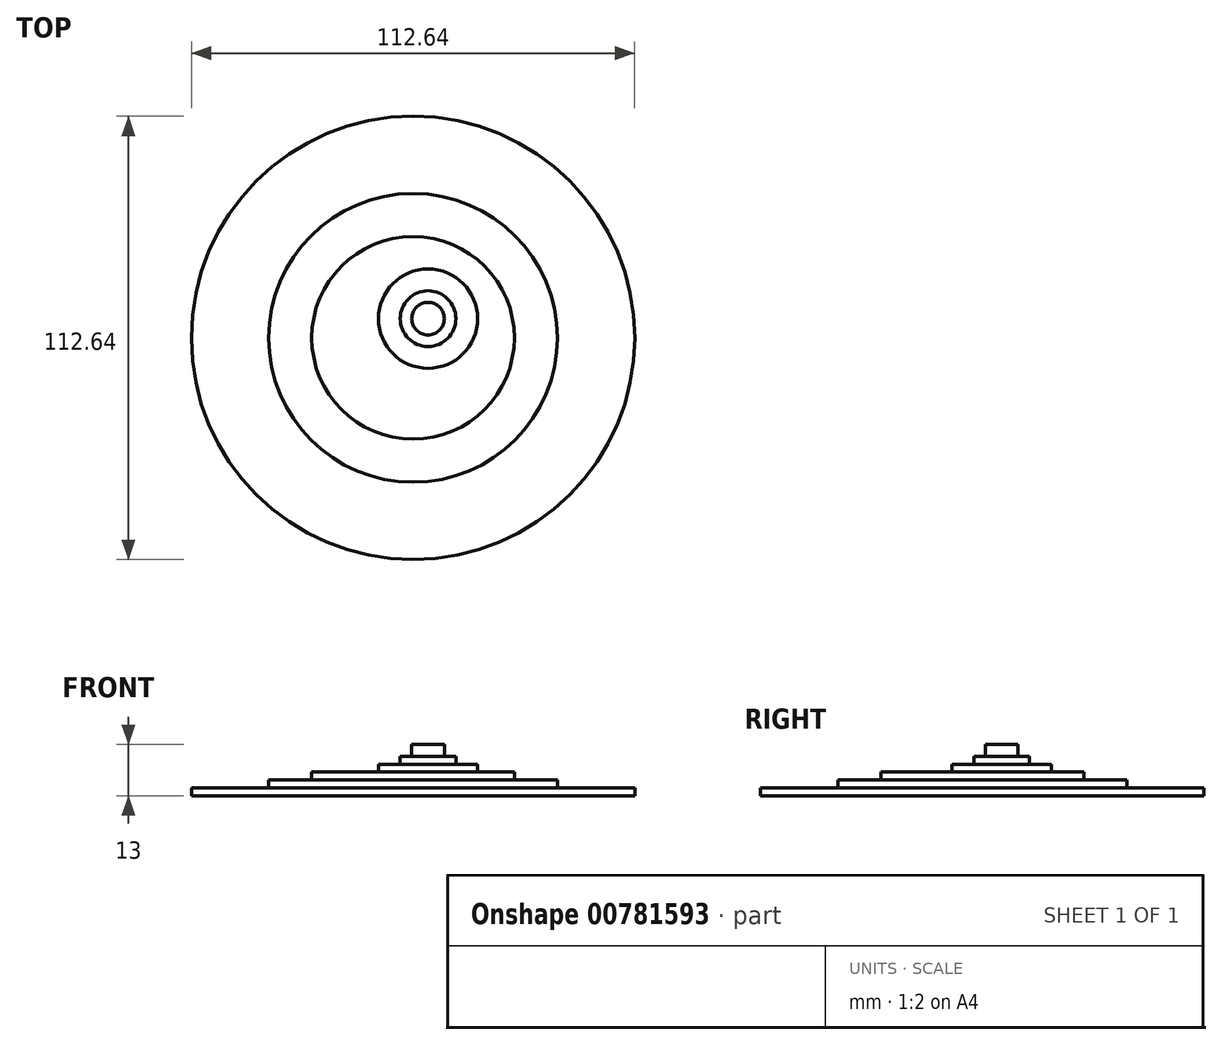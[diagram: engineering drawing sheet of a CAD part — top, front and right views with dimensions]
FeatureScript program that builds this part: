
annotation { "Feature Type Name" : "Feature", "Feature Type Description" : "" }
export const myFeature = defineFeature(function(context is Context, id is Id, definition is map)
    precondition{}
    {
        {
            var Q0;
            Q0=qCreatedBy(makeId("Top.planeOp"),FACE);
            var sketch = newSketch(context, id + "F0", { "sketchPlane" : qUnion([Q0])});
            skCircle(sketch, "E0", {"center": v(0, 0) * mm, "radius": 56.32 * mm});
            skSolve(sketch);
        }
        {
            var Q0;
            Q0=makeQuery(id+"F0.imprint","IMPRINT",FACE,{"disambiguationData":[TD([[makeQuery(id+"F0.imprint","IMPRINT",EDGE,{"derivedFrom":sQuery(id+"F0.wireOp",EDGE,"E0")}),1.0]])]});
            extrude(context, id + "F1", {"entities" : qUnion([Q0]), "depth" : 2 * mm, "offsetDistance" : 25.4 * mm});
        }
        {
            var Q0;
            Q0=makeQuery(id+"F1.opExtrude","CAP_FACE",FACE,{"disambiguationData":[OSD([sQuery(id+"F0.wireOp",EDGE,"E0")])],"isStart":false});
            var sketch = newSketch(context, id + "F2", { "sketchPlane" : qUnion([Q0])});
            skCircle(sketch, "E1", {"center": v(0, 0) * mm, "radius": 36.67 * mm});
            skSolve(sketch);
        }
        {
            var Q0;
            Q0=makeQuery(id+"F2.imprint","IMPRINT",FACE,{"disambiguationData":[TD([[makeQuery(id+"F2.imprint","IMPRINT",EDGE,{"derivedFrom":sQuery(id+"F2.wireOp",EDGE,"E1")}),1.0]])]});
            extrude(context, id + "F3", {"entities" : qUnion([Q0]), "operationType" : NewBodyOperationType.ADD, "depth" : 2 * mm, "offsetDistance" : 25.4 * mm});
        }
        {
            var Q0;
            Q0=makeQuery(id+"F3.opExtrude","CAP_FACE",FACE,{"disambiguationData":[OSD([sQuery(id+"F2.wireOp",EDGE,"E1")])],"isStart":false});
            var sketch = newSketch(context, id + "F4", { "sketchPlane" : qUnion([Q0])});
            skCircle(sketch, "E2", {"center": v(0, 0) * mm, "radius": 25.73 * mm});
            skSolve(sketch);
        }
        {
            var Q0;
            Q0=makeQuery(id+"F4.imprint","IMPRINT",FACE,{"disambiguationData":[TD([[makeQuery(id+"F4.imprint","IMPRINT",EDGE,{"derivedFrom":sQuery(id+"F4.wireOp",EDGE,"E2")}),1.0]])]});
            extrude(context, id + "F5", {"entities" : qUnion([Q0]), "operationType" : NewBodyOperationType.ADD, "depth" : 2 * mm, "offsetDistance" : 25.4 * mm});
        }
        {
            var Q0;
            Q0=makeQuery(id+"F5.opExtrude","CAP_FACE",FACE,{"disambiguationData":[OSD([sQuery(id+"F4.wireOp",EDGE,"E2")])],"isStart":false});
            var sketch = newSketch(context, id + "F6", { "sketchPlane" : qUnion([Q0])});
            skCircle(sketch, "E3", {"center": v(3.81, 4.88) * mm, "radius": 12.6 * mm});
            skSolve(sketch);
        }
        {
            var Q0;
            Q0=makeQuery(id+"F6.imprint","IMPRINT",FACE,{"disambiguationData":[TD([[makeQuery(id+"F6.imprint","IMPRINT",EDGE,{"derivedFrom":sQuery(id+"F6.wireOp",EDGE,"E3")}),1.0]])]});
            extrude(context, id + "F7", {"entities" : qUnion([Q0]), "operationType" : NewBodyOperationType.ADD, "depth" : 2 * mm, "offsetDistance" : 25.4 * mm});
        }
        {
            var Q0;
            Q0=makeQuery(id+"F7.opExtrude","CAP_FACE",FACE,{"disambiguationData":[OSD([sQuery(id+"F6.wireOp",EDGE,"E3")])],"isStart":false});
            var sketch = newSketch(context, id + "F8", { "sketchPlane" : qUnion([Q0])});
            skCircle(sketch, "E4", {"center": v(3.81, 4.88) * mm, "radius": 7.08 * mm});
            skSolve(sketch);
        }
        {
            var Q0;
            Q0=makeQuery(id+"F8.imprint","IMPRINT",FACE,{"disambiguationData":[TD([[makeQuery(id+"F8.imprint","IMPRINT",EDGE,{"derivedFrom":sQuery(id+"F8.wireOp",EDGE,"E4")}),1.0]])]});
            extrude(context, id + "F9", {"entities" : qUnion([Q0]), "operationType" : NewBodyOperationType.ADD, "depth" : 2 * mm, "offsetDistance" : 25.4 * mm});
        }
        {
            var Q0;
            Q0=makeQuery(id+"F9.opExtrude","CAP_FACE",FACE,{"disambiguationData":[OSD([sQuery(id+"F8.wireOp",EDGE,"E4")])],"isStart":false});
            var sketch = newSketch(context, id + "F10", { "sketchPlane" : qUnion([Q0])});
            skCircle(sketch, "E5", {"center": v(3.81, 4.88) * mm, "radius": 4.14 * mm});
            skSolve(sketch);
        }
        {
            var Q0;
            Q0=makeQuery(id+"F10.imprint","IMPRINT",FACE,{"disambiguationData":[TD([[makeQuery(id+"F10.imprint","IMPRINT",EDGE,{"derivedFrom":sQuery(id+"F10.wireOp",EDGE,"E5")}),1.0]])]});
            extrude(context, id + "F11", {"entities" : qUnion([Q0]), "operationType" : NewBodyOperationType.ADD, "depth" : 3 * mm, "offsetDistance" : 25.4 * mm});
        }
    });
